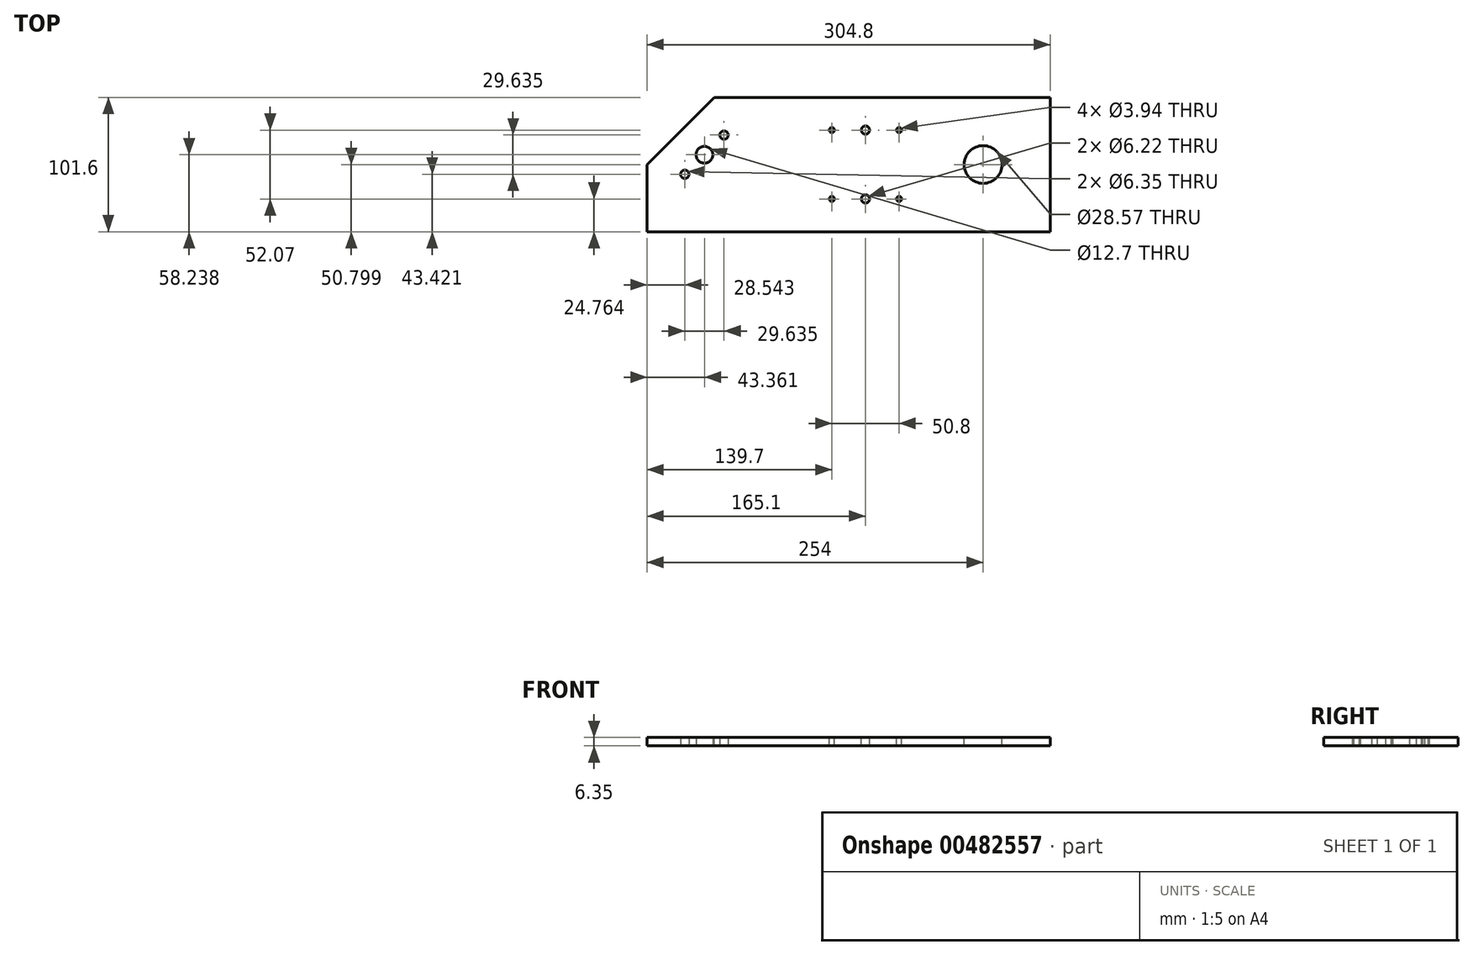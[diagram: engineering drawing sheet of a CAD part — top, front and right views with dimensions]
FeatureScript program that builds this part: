
annotation { "Feature Type Name" : "Feature", "Feature Type Description" : "" }
export const myFeature = defineFeature(function(context is Context, id is Id, definition is map)
    precondition{}
    {
        {
            var Q0;
            Q0=qCreatedBy(makeId("Top.planeOp"),FACE);
            var sketch = newSketch(context, id + "F0", { "sketchPlane" : qUnion([Q0])});
            skLineSegment(sketch, "E0.bottom", {"start": v(-72.69, 42.63) * mm, "end": v(232.11, 42.63) * mm});
            skLineSegment(sketch, "E0.top", {"start": v(-72.69, -58.97) * mm, "end": v(232.11, -58.97) * mm});
            skLineSegment(sketch, "E0.left", {"start": v(-72.69, 42.63) * mm, "end": v(-72.69, -58.97) * mm});
            skLineSegment(sketch, "E0.right", {"start": v(232.11, 42.63) * mm, "end": v(232.11, -58.97) * mm});
            skSolve(sketch);
        }
        {
            var Q0;
            Q0=makeQuery(id+"F0.imprint","IMPRINT",FACE,{"disambiguationData":[TD([[makeQuery(id+"F0.imprint","IMPRINT",EDGE,{"derivedFrom":sQuery(id+"F0.wireOp",EDGE,"E0.bottom")}),-1.0]])]});
            extrude(context, id + "F1", {"entities" : qUnion([Q0]), "depth" : 6.35 * mm});
        }
        {
            var Q0;
            Q0=makeQuery(id+"F1.opExtrude","CAP_FACE",FACE,{"disambiguationData":[OSD([sQuery(id+"F0.wireOp",EDGE,"E0.bottom"),sQuery(id+"F0.wireOp",EDGE,"E0.top"),sQuery(id+"F0.wireOp",EDGE,"E0.left"),sQuery(id+"F0.wireOp",EDGE,"E0.right")])],"isStart":false});
            var sketch = newSketch(context, id + "F2", { "sketchPlane" : qUnion([Q0])});
            skLineSegment(sketch, "E1.bottom", {"start": v(33.3, 1.35) * mm, "end": v(75.32, 1.35) * mm});
            skLineSegment(sketch, "E1.top", {"start": v(33.3, -43.1) * mm, "end": v(75.32, -43.1) * mm});
            skLineSegment(sketch, "E1.left", {"start": v(33.3, 1.35) * mm, "end": v(33.3, -43.1) * mm});
            skLineSegment(sketch, "E1.right", {"start": v(75.32, 1.35) * mm, "end": v(75.32, -43.1) * mm});
            skSolve(sketch);
        }
        {
            var Q0;
            Q0=makeQuery(id+"F2.imprint","IMPRINT",FACE,{"disambiguationData":[TD([[makeQuery(id+"F2.imprint","IMPRINT",EDGE,{"derivedFrom":sQuery(id+"F2.wireOp",EDGE,"E1.bottom")}),1.0]])]});
            var sketch = newSketch(context, id + "F3", { "sketchPlane" : qUnion([Q0])});
            skCircle(sketch, "E2", {"center": v(181.31, -8.17) * mm, "radius": 14.29 * mm});
            skSolve(sketch);
        }
        {
            var Q0;
            Q0=makeQuery(id+"F3.imprint","IMPRINT",FACE,{"disambiguationData":[TD([[makeQuery(id+"F3.imprint","IMPRINT",EDGE,{"derivedFrom":sQuery(id+"F3.wireOp",EDGE,"E2")}),1.0]])]});
            extrude(context, id + "F4", {"entities" : qUnion([Q0]), "operationType" : NewBodyOperationType.REMOVE, "oppositeDirection" : true, "depth" : 6.35 * mm});
        }
        {
            var Q0;
            Q0=makeQuery(id+"F1.opExtrude","CAP_FACE",FACE,{"disambiguationData":[OSD([sQuery(id+"F0.wireOp",EDGE,"E0.bottom"),sQuery(id+"F0.wireOp",EDGE,"E0.top"),sQuery(id+"F0.wireOp",EDGE,"E0.left"),sQuery(id+"F0.wireOp",EDGE,"E0.right")])],"isStart":false});
            var sketch = newSketch(context, id + "F5", { "sketchPlane" : qUnion([Q0])});
            skCircle(sketch, "E3", {"center": v(92.41, 17.86) * mm, "radius": 3.11 * mm});
            skSolve(sketch);
        }
        {
            var Q0;
            Q0=makeQuery(id+"F5.imprint","IMPRINT",FACE,{"disambiguationData":[TD([[makeQuery(id+"F5.imprint","IMPRINT",EDGE,{"derivedFrom":sQuery(id+"F5.wireOp",EDGE,"E3")}),-1.0]])]});
            var sketch = newSketch(context, id + "F6", { "sketchPlane" : qUnion([Q0])});
            skCircle(sketch, "E4", {"center": v(92.41, -34.2) * mm, "radius": 3.11 * mm});
            skSolve(sketch);
        }
        {
            var Q0;
            Q0=makeQuery(id+"F5.imprint","IMPRINT",FACE,{"disambiguationData":[TD([[makeQuery(id+"F5.imprint","IMPRINT",EDGE,{"derivedFrom":sQuery(id+"F5.wireOp",EDGE,"E3")}),-1.0]])]});
            var sketch = newSketch(context, id + "F7", { "sketchPlane" : qUnion([Q0])});
            skCircle(sketch, "E5", {"center": v(117.81, 17.86) * mm, "radius": 1.97 * mm});
            skSolve(sketch);
        }
        {
            var Q0;
            Q0=makeQuery(id+"F6.imprint","IMPRINT",FACE,{"disambiguationData":[TD([[makeQuery(id+"F6.imprint","IMPRINT",EDGE,{"derivedFrom":sQuery(id+"F6.wireOp",EDGE,"E4")}),-1.0]])]});
            var sketch = newSketch(context, id + "F8", { "sketchPlane" : qUnion([Q0])});
            skCircle(sketch, "E6", {"center": v(67.01, 17.86) * mm, "radius": 1.97 * mm});
            skSolve(sketch);
        }
        {
            var Q0;
            Q0=makeQuery(id+"F5.imprint","IMPRINT",FACE,{"disambiguationData":[TD([[makeQuery(id+"F5.imprint","IMPRINT",EDGE,{"derivedFrom":sQuery(id+"F5.wireOp",EDGE,"E3")}),1.0]])]});
            extrude(context, id + "F9", {"entities" : qUnion([Q0]), "operationType" : NewBodyOperationType.REMOVE, "oppositeDirection" : true, "depth" : 6.35 * mm});
        }
        {
            var Q0;
            Q0=makeQuery(id+"F6.imprint","IMPRINT",FACE,{"disambiguationData":[TD([[makeQuery(id+"F6.imprint","IMPRINT",EDGE,{"derivedFrom":sQuery(id+"F6.wireOp",EDGE,"E4")}),1.0]])]});
            extrude(context, id + "F10", {"entities" : qUnion([Q0]), "operationType" : NewBodyOperationType.REMOVE, "oppositeDirection" : true, "depth" : 6.35 * mm});
        }
        {
            var Q0;
            Q0=makeQuery(id+"F7.imprint","IMPRINT",FACE,{"disambiguationData":[TD([[makeQuery(id+"F7.imprint","IMPRINT",EDGE,{"derivedFrom":sQuery(id+"F7.wireOp",EDGE,"E5")}),1.0]])]});
            extrude(context, id + "F11", {"entities" : qUnion([Q0]), "operationType" : NewBodyOperationType.REMOVE, "oppositeDirection" : true, "depth" : 6.35 * mm});
        }
        {
            var Q0;
            Q0=makeQuery(id+"F8.imprint","IMPRINT",FACE,{"disambiguationData":[TD([[makeQuery(id+"F8.imprint","IMPRINT",EDGE,{"derivedFrom":sQuery(id+"F8.wireOp",EDGE,"E6")}),1.0]])]});
            extrude(context, id + "F12", {"entities" : qUnion([Q0]), "operationType" : NewBodyOperationType.REMOVE, "oppositeDirection" : true, "depth" : 6.35 * mm});
        }
        {
            var Q0;
            Q0=makeQuery(id+"F1.opExtrude","CAP_FACE",FACE,{"disambiguationData":[OSD([sQuery(id+"F0.wireOp",EDGE,"E0.bottom"),sQuery(id+"F0.wireOp",EDGE,"E0.top"),sQuery(id+"F0.wireOp",EDGE,"E0.left"),sQuery(id+"F0.wireOp",EDGE,"E0.right")])],"isStart":false});
            var sketch = newSketch(context, id + "F13", { "sketchPlane" : qUnion([Q0])});
            skCircle(sketch, "E7", {"center": v(67.01, -34.2) * mm, "radius": 1.97 * mm});
            skSolve(sketch);
        }
        {
            var Q0;
            Q0=makeQuery(id+"F6.imprint","IMPRINT",FACE,{"disambiguationData":[TD([[makeQuery(id+"F6.imprint","IMPRINT",EDGE,{"derivedFrom":sQuery(id+"F6.wireOp",EDGE,"E4")}),-1.0]])]});
            var sketch = newSketch(context, id + "F14", { "sketchPlane" : qUnion([Q0])});
            skCircle(sketch, "E8", {"center": v(117.81, -34.2) * mm, "radius": 1.97 * mm});
            skSolve(sketch);
        }
        {
            var Q0;
            Q0=makeQuery(id+"F6.imprint","IMPRINT",FACE,{"disambiguationData":[TD([[makeQuery(id+"F6.imprint","IMPRINT",EDGE,{"derivedFrom":sQuery(id+"F6.wireOp",EDGE,"E4")}),1.0]])]});
            extrude(context, id + "F15", {"entities" : qUnion([Q0]), "operationType" : NewBodyOperationType.REMOVE, "oppositeDirection" : true, "depth" : 6.35 * mm});
        }
        {
            var Q0;
            Q0=makeQuery(id+"F13.imprint","IMPRINT",FACE,{"disambiguationData":[TD([[makeQuery(id+"F13.imprint","IMPRINT",EDGE,{"derivedFrom":sQuery(id+"F13.wireOp",EDGE,"E7")}),1.0]])]});
            extrude(context, id + "F16", {"entities" : qUnion([Q0]), "operationType" : NewBodyOperationType.REMOVE, "oppositeDirection" : true, "depth" : 6.35 * mm});
        }
        {
            var Q0;
            Q0=makeQuery(id+"F14.imprint","IMPRINT",FACE,{"disambiguationData":[TD([[makeQuery(id+"F14.imprint","IMPRINT",EDGE,{"derivedFrom":sQuery(id+"F14.wireOp",EDGE,"E8")}),1.0]])]});
            extrude(context, id + "F17", {"entities" : qUnion([Q0]), "operationType" : NewBodyOperationType.REMOVE, "oppositeDirection" : true, "depth" : 6.35 * mm});
        }
        {
            var Q0;
            Q0=makeQuery(id+"F1.opExtrude","SWEPT_EDGE",EDGE,{"disambiguationData":[OSD([sQuery(id+"F0.wireOp",EDGE,"E0.bottom"),sQuery(id+"F0.wireOp",EDGE,"E0.left")])]});
            chamfer(context, id + "F18", {"entities" : qUnion([Q0]), "width" : 50.8 * mm, "tangentPropagation" : true});
        }
        {
            var Q0;
            Q0=makeQuery(id+"F1.opExtrude","CAP_FACE",FACE,{"disambiguationData":[OSD([sQuery(id+"F0.wireOp",EDGE,"E0.bottom"),sQuery(id+"F0.wireOp",EDGE,"E0.top"),sQuery(id+"F0.wireOp",EDGE,"E0.left"),sQuery(id+"F0.wireOp",EDGE,"E0.right")])],"isStart":true});
            var sketch = newSketch(context, id + "F19", { "sketchPlane" : qUnion([Q0])});
            skLineSegment(sketch, "E9", {"start": v(-47.29, -17.23) * mm, "end": v(28.91, 58.97) * mm});
            skCircle(sketch, "E10", {"center": v(-29.33, 0.73) * mm, "radius": 6.35 * mm});
            skLineSegment(sketch, "E11", {"start": v(-29.33, 0.73) * mm, "end": v(-44.15, 15.55) * mm});
            skLineSegment(sketch, "E12", {"start": v(-29.33, 0.73) * mm, "end": v(-14.51, -14.09) * mm});
            skCircle(sketch, "E13", {"center": v(-14.51, -14.09) * mm, "radius": 3.18 * mm});
            skCircle(sketch, "E14", {"center": v(-44.15, 15.55) * mm, "radius": 3.18 * mm});
            skSolve(sketch);
        }
        {
            var Q0;
            {var subQ0=sQuery(id+"F19.wireOp",EDGE,"E11");var subQ3=sQuery(id+"F19.wireOp",EDGE,"E10");var subQ5=makeQuery(id+"F19.imprint","INTERSECT",VERTEX,{"derivedFrom":[subQ3,subQ0]});Q0=makeQuery(id+"F19.imprint","IMPRINT",FACE,{"disambiguationData":[TD([[makeQuery(id+"F19.imprint","IMPRINT",EDGE,{"disambiguationData":[TD([[subQ5,-1.0]])],"derivedFrom":subQ3}),1.0]])]});}
            var Q1;
            {var subQ0=sQuery(id+"F19.wireOp",EDGE,"E12");var subQ3=sQuery(id+"F19.wireOp",EDGE,"E10");var subQ5=makeQuery(id+"F19.imprint","INTERSECT",VERTEX,{"derivedFrom":[subQ3,subQ0]});Q1=makeQuery(id+"F19.imprint","IMPRINT",FACE,{"disambiguationData":[TD([[makeQuery(id+"F19.imprint","IMPRINT",EDGE,{"disambiguationData":[TD([[subQ5,1.0]])],"derivedFrom":subQ3}),1.0]])]});}
            var Q2;
            {var subQ0=sQuery(id+"F19.wireOp",EDGE,"E12");var subQ3=sQuery(id+"F19.wireOp",EDGE,"E10");var subQ5=makeQuery(id+"F19.imprint","INTERSECT",VERTEX,{"derivedFrom":[subQ3,subQ0]});Q2=makeQuery(id+"F19.imprint","IMPRINT",FACE,{"disambiguationData":[TD([[makeQuery(id+"F19.imprint","IMPRINT",EDGE,{"disambiguationData":[TD([[subQ5,-1.0]])],"derivedFrom":subQ3}),1.0]])]});}
            var Q3;
            Q3=makeQuery(id+"F19.imprint","IMPRINT",FACE,{"disambiguationData":[TD([[makeQuery(id+"F19.imprint","IMPRINT",EDGE,{"derivedFrom":sQuery(id+"F19.wireOp",EDGE,"E13")}),1.0]])]});
            var Q4;
            Q4=makeQuery(id+"F19.imprint","IMPRINT",FACE,{"disambiguationData":[TD([[makeQuery(id+"F19.imprint","IMPRINT",EDGE,{"derivedFrom":sQuery(id+"F19.wireOp",EDGE,"E14")}),1.0]])]});
            var Q5;
            {var subQ0=sQuery(id+"F19.wireOp",EDGE,"E11");var subQ3=sQuery(id+"F19.wireOp",EDGE,"E10");var subQ5=makeQuery(id+"F19.imprint","INTERSECT",VERTEX,{"derivedFrom":[subQ3,subQ0]});Q5=makeQuery(id+"F19.imprint","IMPRINT",FACE,{"disambiguationData":[TD([[makeQuery(id+"F19.imprint","IMPRINT",EDGE,{"disambiguationData":[TD([[subQ5,1.0]])],"derivedFrom":subQ3}),1.0]])]});}
            extrude(context, id + "F20", {"entities" : qUnion([Q0, Q1, Q2, Q3, Q4, Q5]), "operationType" : NewBodyOperationType.REMOVE, "oppositeDirection" : true, "depth" : 6.35 * mm, "offsetDistance" : 25.4 * mm});
        }
    });
